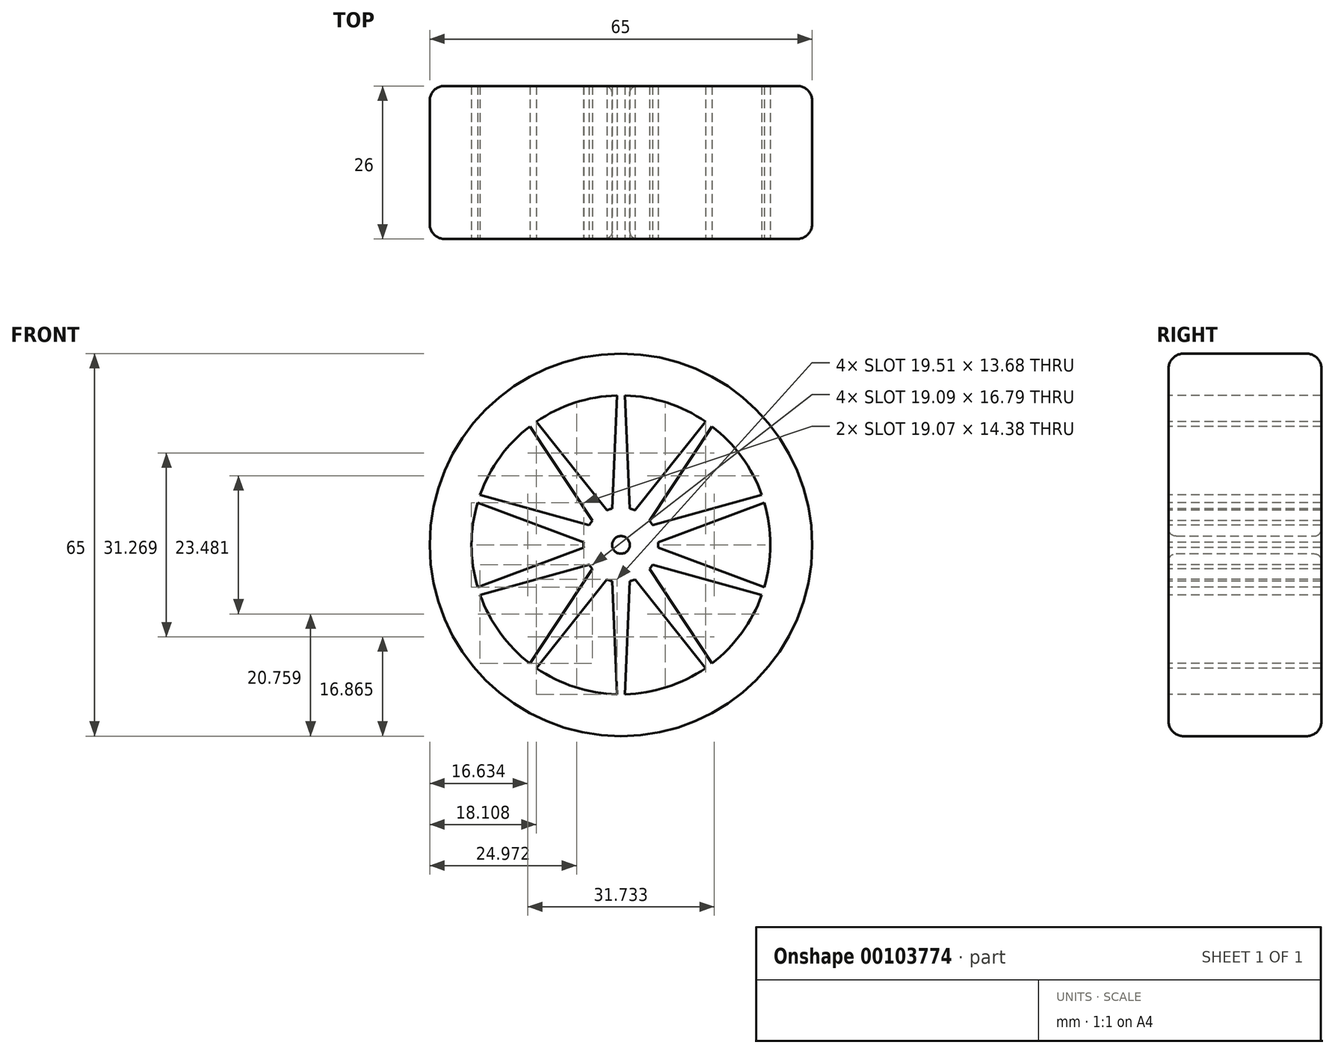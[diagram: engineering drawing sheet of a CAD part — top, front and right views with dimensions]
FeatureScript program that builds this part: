
annotation { "Feature Type Name" : "Feature", "Feature Type Description" : "" }
export const myFeature = defineFeature(function(context is Context, id is Id, definition is map)
    precondition{}
    {
        {
            var Q0;
            Q0=qCreatedBy(makeId("Front.planeOp"),FACE);
            var sketch = newSketch(context, id + "F0", { "sketchPlane" : qUnion([Q0])});
            skCircle(sketch, "E0", {"center": v(0, 0) * mm, "radius": 32.5 * mm});
            skCircle(sketch, "E1", {"center": v(0, 0) * mm, "radius": 1.5 * mm});
            skSolve(sketch);
        }
        {
            var Q0;
            Q0=makeQuery(id+"F0.imprint","IMPRINT",FACE,{"disambiguationData":[TD([[makeQuery(id+"F0.imprint","IMPRINT",EDGE,{"derivedFrom":sQuery(id+"F0.wireOp",EDGE,"E0")}),1.0]])]});
            extrude(context, id + "F1", {"entities" : qUnion([Q0]), "depth" : 26 * mm});
        }
        {
            var Q0;
            Q0=makeQuery(id+"F1.opExtrude","CAP_EDGE",EDGE,{"disambiguationData":[OSD([sQuery(id+"F0.wireOp",EDGE,"E0")])],"isStart":false});
            var Q1;
            Q1=makeQuery(id+"F1.opExtrude","CAP_EDGE",EDGE,{"disambiguationData":[OSD([sQuery(id+"F0.wireOp",EDGE,"E0")])],"isStart":true});
            fillet(context, id + "F2", {"entities" : qUnion([Q0, Q1]), "radius" : 2.54 * mm, "tangentPropagation" : true, "allowEdgeOverflow" : false});
        }
        {
            var Q0;
            Q0=makeQuery(id+"F1.opExtrude","CAP_FACE",FACE,{"disambiguationData":[OSD([sQuery(id+"F0.wireOp",EDGE,"E0"),sQuery(id+"F0.wireOp",EDGE,"E1")])],"isStart":false});
            var sketch = newSketch(context, id + "F3", { "sketchPlane" : qUnion([Q0])});
            skCircle(sketch, "E2", {"center": v(0, 0) * mm, "radius": 25.4 * mm});
            skCircle(sketch, "E3", {"center": v(0, 0) * mm, "radius": 6.35 * mm});
            skLineSegment(sketch, "E4", {"start": v(-3.73, 5.14) * mm, "end": v(-2.4, 5.88) * mm});
            skLineSegment(sketch, "E5", {"start": v(-3.73, 5.14) * mm, "end": v(-4.85, 4.1) * mm});
            skLineSegment(sketch, "E6.1.0", {"start": v(-6.04, 1.96) * mm, "end": v(-5.4, 3.34) * mm});
            skLineSegment(sketch, "E6.2.0", {"start": v(-6.04, -1.96) * mm, "end": v(-6.33, -0.47) * mm});
            skLineSegment(sketch, "E6.3.0", {"start": v(-3.73, -5.14) * mm, "end": v(-4.85, -4.1) * mm});
            skLineSegment(sketch, "E6.4.0", {"start": v(0, -6.35) * mm, "end": v(-1.51, -6.17) * mm});
            skLineSegment(sketch, "E6.5.0", {"start": v(3.73, -5.14) * mm, "end": v(2.4, -5.88) * mm});
            skLineSegment(sketch, "E6.6.0", {"start": v(6.04, -1.96) * mm, "end": v(5.4, -3.34) * mm});
            skLineSegment(sketch, "E6.7.0", {"start": v(6.04, 1.96) * mm, "end": v(6.33, 0.47) * mm});
            skLineSegment(sketch, "E6.8.0", {"start": v(3.73, 5.14) * mm, "end": v(4.85, 4.1) * mm});
            skLineSegment(sketch, "E6.9.0", {"start": v(0, 6.35) * mm, "end": v(1.51, 6.17) * mm});
            skLineSegment(sketch, "E7.1.0", {"start": v(-6.04, 1.96) * mm, "end": v(-6.33, 0.47) * mm});
            skLineSegment(sketch, "E7.2.0", {"start": v(-6.04, -1.96) * mm, "end": v(-5.4, -3.34) * mm});
            skLineSegment(sketch, "E7.3.0", {"start": v(-3.73, -5.14) * mm, "end": v(-2.4, -5.88) * mm});
            skLineSegment(sketch, "E7.4.0", {"start": v(0, -6.35) * mm, "end": v(1.51, -6.17) * mm});
            skLineSegment(sketch, "E7.5.0", {"start": v(3.73, -5.14) * mm, "end": v(4.85, -4.1) * mm});
            skLineSegment(sketch, "E7.6.0", {"start": v(6.04, -1.96) * mm, "end": v(6.33, -0.47) * mm});
            skLineSegment(sketch, "E7.7.0", {"start": v(6.04, 1.96) * mm, "end": v(5.4, 3.34) * mm});
            skLineSegment(sketch, "E7.8.0", {"start": v(3.73, 5.14) * mm, "end": v(2.4, 5.88) * mm});
            skLineSegment(sketch, "E7.9.0", {"start": v(0, 6.35) * mm, "end": v(-1.51, 6.17) * mm});
            skLineSegment(sketch, "E8", {"start": v(-2.4, 5.88) * mm, "end": v(-14.37, 20.95) * mm});
            skLineSegment(sketch, "E9.MirrorCS", {"start": v(-4.85, 4.1) * mm, "end": v(-15.48, 20.14) * mm});
            skPoint(sketch, "E10.start.orphan", {"position": v(0, 6.35) * mm});
            skLineSegment(sketch, "E11.1.0", {"start": v(-5.4, 3.34) * mm, "end": v(-23.94, 8.5) * mm});
            skLineSegment(sketch, "E11.2.0", {"start": v(-6.33, -0.47) * mm, "end": v(-24.36, -7.2) * mm});
            skLineSegment(sketch, "E11.3.0", {"start": v(-4.85, -4.1) * mm, "end": v(-15.48, -20.14) * mm});
            skLineSegment(sketch, "E11.4.0", {"start": v(-1.51, -6.17) * mm, "end": v(-0.69, -25.4) * mm});
            skLineSegment(sketch, "E11.5.0", {"start": v(2.4, -5.88) * mm, "end": v(14.37, -20.95) * mm});
            skLineSegment(sketch, "E11.6.0", {"start": v(5.4, -3.34) * mm, "end": v(23.94, -8.5) * mm});
            skLineSegment(sketch, "E11.7.0", {"start": v(6.33, 0.47) * mm, "end": v(24.36, 7.2) * mm});
            skLineSegment(sketch, "E11.8.0", {"start": v(4.85, 4.1) * mm, "end": v(15.48, 20.14) * mm});
            skLineSegment(sketch, "E11.9.0", {"start": v(1.51, 6.17) * mm, "end": v(0.69, 25.4) * mm});
            skLineSegment(sketch, "E12.1.0", {"start": v(-6.33, 0.47) * mm, "end": v(-24.36, 7.2) * mm});
            skLineSegment(sketch, "E12.2.0", {"start": v(-5.4, -3.34) * mm, "end": v(-23.94, -8.5) * mm});
            skLineSegment(sketch, "E12.3.0", {"start": v(-2.4, -5.88) * mm, "end": v(-14.37, -20.95) * mm});
            skLineSegment(sketch, "E12.4.0", {"start": v(1.51, -6.17) * mm, "end": v(0.69, -25.4) * mm});
            skLineSegment(sketch, "E12.5.0", {"start": v(4.85, -4.1) * mm, "end": v(15.48, -20.14) * mm});
            skLineSegment(sketch, "E12.6.0", {"start": v(6.33, -0.47) * mm, "end": v(24.36, -7.2) * mm});
            skLineSegment(sketch, "E12.7.0", {"start": v(5.4, 3.34) * mm, "end": v(23.94, 8.5) * mm});
            skLineSegment(sketch, "E12.8.0", {"start": v(2.4, 5.88) * mm, "end": v(14.37, 20.95) * mm});
            skLineSegment(sketch, "E12.9.0", {"start": v(-1.51, 6.17) * mm, "end": v(-0.69, 25.4) * mm});
            skSolve(sketch);
        }
        {
            var Q0;
            {var subQ0=sQuery(id+"F3.wireOp",EDGE,"E8");Q0=makeQuery(id+"F3.imprint","IMPRINT",FACE,{"disambiguationData":[TD([[makeQuery(id+"F3.imprint","IMPRINT",EDGE,{"derivedFrom":subQ0}),-1.0]])]});}
            var Q1;
            {var subQ0=sQuery(id+"F3.wireOp",EDGE,"E11.9.0");Q1=makeQuery(id+"F3.imprint","IMPRINT",FACE,{"disambiguationData":[TD([[makeQuery(id+"F3.imprint","IMPRINT",EDGE,{"derivedFrom":subQ0}),-1.0]])]});}
            var Q2;
            {var subQ0=sQuery(id+"F3.wireOp",EDGE,"E11.8.0");Q2=makeQuery(id+"F3.imprint","IMPRINT",FACE,{"disambiguationData":[TD([[makeQuery(id+"F3.imprint","IMPRINT",EDGE,{"derivedFrom":subQ0}),-1.0]])]});}
            var Q3;
            {var subQ0=sQuery(id+"F3.wireOp",EDGE,"E11.7.0");Q3=makeQuery(id+"F3.imprint","IMPRINT",FACE,{"disambiguationData":[TD([[makeQuery(id+"F3.imprint","IMPRINT",EDGE,{"derivedFrom":subQ0}),-1.0]])]});}
            var Q4;
            {var subQ0=sQuery(id+"F3.wireOp",EDGE,"E11.6.0");Q4=makeQuery(id+"F3.imprint","IMPRINT",FACE,{"disambiguationData":[TD([[makeQuery(id+"F3.imprint","IMPRINT",EDGE,{"derivedFrom":subQ0}),-1.0]])]});}
            var Q5;
            {var subQ0=sQuery(id+"F3.wireOp",EDGE,"E11.5.0");Q5=makeQuery(id+"F3.imprint","IMPRINT",FACE,{"disambiguationData":[TD([[makeQuery(id+"F3.imprint","IMPRINT",EDGE,{"derivedFrom":subQ0}),-1.0]])]});}
            var Q6;
            {var subQ0=sQuery(id+"F3.wireOp",EDGE,"E11.4.0");Q6=makeQuery(id+"F3.imprint","IMPRINT",FACE,{"disambiguationData":[TD([[makeQuery(id+"F3.imprint","IMPRINT",EDGE,{"derivedFrom":subQ0}),-1.0]])]});}
            var Q7;
            {var subQ0=sQuery(id+"F3.wireOp",EDGE,"E11.3.0");Q7=makeQuery(id+"F3.imprint","IMPRINT",FACE,{"disambiguationData":[TD([[makeQuery(id+"F3.imprint","IMPRINT",EDGE,{"derivedFrom":subQ0}),-1.0]])]});}
            var Q8;
            {var subQ0=sQuery(id+"F3.wireOp",EDGE,"E11.2.0");Q8=makeQuery(id+"F3.imprint","IMPRINT",FACE,{"disambiguationData":[TD([[makeQuery(id+"F3.imprint","IMPRINT",EDGE,{"derivedFrom":subQ0}),-1.0]])]});}
            var Q9;
            {var subQ0=sQuery(id+"F3.wireOp",EDGE,"E9.MirrorCS");Q9=makeQuery(id+"F3.imprint","IMPRINT",FACE,{"disambiguationData":[TD([[makeQuery(id+"F3.imprint","IMPRINT",EDGE,{"derivedFrom":subQ0}),1.0]])]});}
            extrude(context, id + "F4", {"entities" : qUnion([Q0, Q1, Q2, Q3, Q4, Q5, Q6, Q7, Q8, Q9]), "operationType" : NewBodyOperationType.REMOVE, "oppositeDirection" : true, "depth" : 50.8 * mm});
        }
        {
            var Q0;
            Q0=makeQuery(id+"F1.opExtrude","CAP_EDGE",EDGE,{"disambiguationData":[OSD([sQuery(id+"F0.wireOp",EDGE,"E1")])],"isStart":false});
            var Q1;
            Q1=makeQuery(id+"F1.opExtrude","CAP_EDGE",EDGE,{"disambiguationData":[OSD([sQuery(id+"F0.wireOp",EDGE,"E1")])],"isStart":true});
            fillet(context, id + "F5", {"entities" : qUnion([Q0, Q1]), "radius" : 1.27 * mm, "tangentPropagation" : true, "allowEdgeOverflow" : false});
        }
    });
